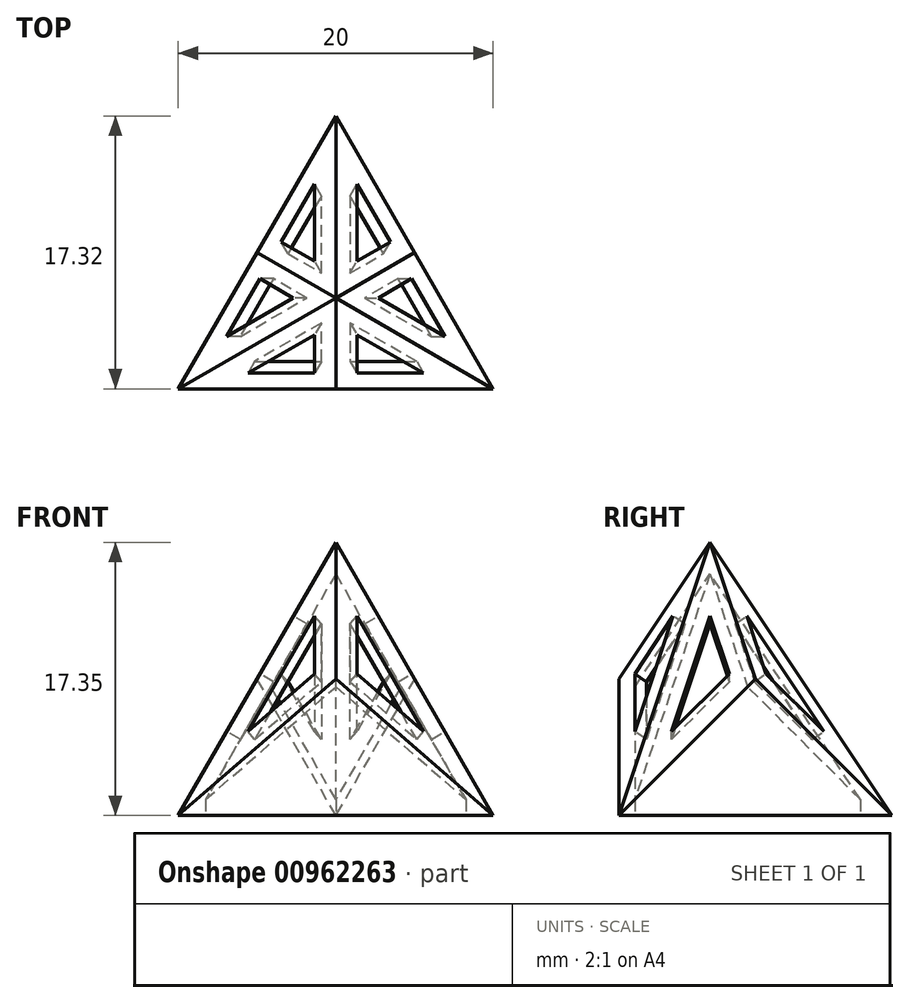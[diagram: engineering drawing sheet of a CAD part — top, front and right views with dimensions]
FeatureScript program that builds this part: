
annotation { "Feature Type Name" : "Feature", "Feature Type Description" : "" }
export const myFeature = defineFeature(function(context is Context, id is Id, definition is map)
    precondition{}
    {
        {
            var Q0;
            Q0=qCreatedBy(makeId("Top.planeOp"),FACE);
            var sketch = newSketch(context, id + "F0", { "sketchPlane" : qUnion([Q0])});
            skLineSegment(sketch, "E0", {"start": v(-10, -5.77) * mm, "end": v(0, 11.55) * mm});
            skLineSegment(sketch, "E1", {"start": v(0, 11.55) * mm, "end": v(10, -5.77) * mm});
            skLineSegment(sketch, "E2", {"start": v(10, -5.77) * mm, "end": v(-10, -5.77) * mm});
            skLineSegment(sketch, "E3", {"start": v(0, 0) * mm, "end": v(0, 11.55) * mm, "construction": true});
            skLineSegment(sketch, "E4", {"start": v(-10, -5.77) * mm, "end": v(0, 0) * mm, "construction": true});
            skLineSegment(sketch, "E5", {"start": v(10, -5.77) * mm, "end": v(0, 0) * mm, "construction": true});
            skSolve(sketch);
        }
        {
            var Q0;
            Q0 = qSketchRegion(id + "F0", true);
            extrude(context, id + "F1", {"entities" : qUnion([Q0]), "depth" : 17.35 * mm, "offsetDistance" : 25.4 * mm});
        }
        {
            var Q0;
            Q0=makeQuery(id+"F1.opExtrude","SWEPT_FACE",FACE,{"disambiguationData":[OSD([sQuery(id+"F0.wireOp",EDGE,"E0")])]});
            var sketch = newSketch(context, id + "F2", { "sketchPlane" : qUnion([Q0])});
            skLineSegment(sketch, "E6", {"start": v(-10, 0) * mm, "end": v(0, 17.35) * mm});
            skLineSegment(sketch, "E7", {"start": v(0, 17.35) * mm, "end": v(10, 0) * mm});
            skLineSegment(sketch, "E8", {"start": v(10, 0) * mm, "end": v(10, 17.35) * mm});
            skLineSegment(sketch, "E9", {"start": v(10, 17.35) * mm, "end": v(-10, 17.35) * mm});
            skLineSegment(sketch, "E10", {"start": v(-10, 17.35) * mm, "end": v(-10, 0) * mm});
            skSolve(sketch);
        }
        {
            var Q0;
            Q0 = qSketchRegion(id + "F2", true);
            extrude(context, id + "F3", {"entities" : qUnion([Q0]), "operationType" : NewBodyOperationType.REMOVE, "endBound" : BoundingType.THROUGH_ALL, "oppositeDirection" : true, "depth" : 25.4 * mm, "offsetDistance" : 25.4 * mm});
        }
        {
            var Q0;
            Q0=makeQuery(id+"F1.opExtrude","SWEPT_FACE",FACE,{"disambiguationData":[OSD([sQuery(id+"F0.wireOp",EDGE,"E2")])]});
            var sketch = newSketch(context, id + "F4", { "sketchPlane" : qUnion([Q0])});
            skLineSegment(sketch, "E11", {"start": v(-10, 0) * mm, "end": v(0, 17.35) * mm});
            skLineSegment(sketch, "E12", {"start": v(0, 17.35) * mm, "end": v(10, 0) * mm});
            skLineSegment(sketch, "E13", {"start": v(10, 0) * mm, "end": v(10, 17.35) * mm});
            skLineSegment(sketch, "E14", {"start": v(10, 17.35) * mm, "end": v(-10, 17.35) * mm});
            skLineSegment(sketch, "E15", {"start": v(-10, 17.35) * mm, "end": v(-10, 0) * mm});
            skSolve(sketch);
        }
        {
            var Q0;
            Q0 = qSketchRegion(id + "F4", true);
            extrude(context, id + "F5", {"entities" : qUnion([Q0]), "operationType" : NewBodyOperationType.REMOVE, "endBound" : BoundingType.THROUGH_ALL, "oppositeDirection" : true, "depth" : 25.4 * mm, "offsetDistance" : 25.4 * mm});
        }
        {
            var Q0;
            Q0=makeQuery(id+"F1.opExtrude","SWEPT_FACE",FACE,{"disambiguationData":[OSD([sQuery(id+"F0.wireOp",EDGE,"E1")])]});
            var sketch = newSketch(context, id + "F6", { "sketchPlane" : qUnion([Q0])});
            skLineSegment(sketch, "E16", {"start": v(-10, 0) * mm, "end": v(0, 17.35) * mm});
            skLineSegment(sketch, "E17", {"start": v(0, 17.35) * mm, "end": v(10, 0) * mm});
            skLineSegment(sketch, "E18", {"start": v(10, 0) * mm, "end": v(10, 17.35) * mm});
            skLineSegment(sketch, "E19", {"start": v(10, 17.35) * mm, "end": v(-10, 17.35) * mm});
            skLineSegment(sketch, "E20", {"start": v(-10, 17.35) * mm, "end": v(-10, 0) * mm});
            skSolve(sketch);
        }
        {
            var Q0;
            Q0 = qSketchRegion(id + "F6", true);
            extrude(context, id + "F7", {"entities" : qUnion([Q0]), "operationType" : NewBodyOperationType.REMOVE, "endBound" : BoundingType.THROUGH_ALL, "oppositeDirection" : true, "depth" : 25.4 * mm, "offsetDistance" : 25.4 * mm});
        }
        {
            var Q0;
            Q0=makeQuery(id+"F1.opExtrude","CAP_FACE",FACE,{"disambiguationData":[OSD([sQuery(id+"F0.wireOp",EDGE,"E0"),sQuery(id+"F0.wireOp",EDGE,"E1"),sQuery(id+"F0.wireOp",EDGE,"E2")])],"isStart":true});
            shell(context, id + "F8", {"entities" : qUnion([Q0]), "thickness" : 1 * mm});
        }
        {
            var Q0;
            Q0=makeQuery(id+"F5.boolean.opBoolean","COPY",FACE,{"derivedFrom":makeQuery(id+"F5.opExtrude","SWEPT_FACE",FACE,{"disambiguationData":[OSD([sQuery(id+"F4.wireOp",EDGE,"E12")])]})});
            var sketch = newSketch(context, id + "F9", { "sketchPlane" : qUnion([Q0])});
            skLineSegment(sketch, "E21.0", {"start": v(1.22, 5.38) * mm, "end": v(0, 9.62) * mm});
            skLineSegment(sketch, "E21.1", {"start": v(-2.44, 1.15) * mm, "end": v(1.22, 5.38) * mm});
            skLineSegment(sketch, "E21.2", {"start": v(0, 9.62) * mm, "end": v(-2.44, 1.15) * mm});
            skSolve(sketch);
        }
        {
            var Q0;
            Q0 = qSketchRegion(id + "F9", true);
            extrude(context, id + "F10", {"entities" : qUnion([Q0]), "operationType" : NewBodyOperationType.REMOVE, "endBound" : BoundingType.UP_TO_NEXT, "oppositeDirection" : true, "depth" : 25.4 * mm, "offsetDistance" : 25.4 * mm});
        }
        {
            var Q0;
            Q0=makeQuery(id+"F7.boolean.opBoolean","COPY",FACE,{"derivedFrom":makeQuery(id+"F7.opExtrude","SWEPT_FACE",FACE,{"disambiguationData":[OSD([sQuery(id+"F6.wireOp",EDGE,"E16")])]})});
            var sketch = newSketch(context, id + "F11", { "sketchPlane" : qUnion([Q0])});
            skLineSegment(sketch, "E22.0", {"start": v(-2.66, 4.84) * mm, "end": v(2.03, 1.78) * mm});
            skLineSegment(sketch, "E22.1", {"start": v(-2.66, 9.24) * mm, "end": v(-2.66, 4.84) * mm});
            skLineSegment(sketch, "E22.2", {"start": v(2.03, 1.78) * mm, "end": v(-2.66, 9.24) * mm});
            skSolve(sketch);
        }
        {
            var Q0;
            Q0 = qSketchRegion(id + "F11", true);
            extrude(context, id + "F12", {"entities" : qUnion([Q0]), "operationType" : NewBodyOperationType.REMOVE, "endBound" : BoundingType.UP_TO_NEXT, "oppositeDirection" : true, "depth" : 25.4 * mm, "offsetDistance" : 25.4 * mm});
        }
        {
            var Q0;
            Q0=makeQuery(id+"F3.boolean.opBoolean","COPY",FACE,{"derivedFrom":makeQuery(id+"F3.opExtrude","SWEPT_FACE",FACE,{"disambiguationData":[OSD([sQuery(id+"F2.wireOp",EDGE,"E7")])]})});
            var sketch = newSketch(context, id + "F13", { "sketchPlane" : qUnion([Q0])});
            skLineSegment(sketch, "E23.0", {"start": v(-2.03, 1.78) * mm, "end": v(2.66, 4.84) * mm});
            skLineSegment(sketch, "E23.1", {"start": v(2.66, 9.24) * mm, "end": v(-2.03, 1.78) * mm});
            skLineSegment(sketch, "E23.2", {"start": v(2.66, 4.84) * mm, "end": v(2.66, 9.24) * mm});
            skSolve(sketch);
        }
        {
            var Q0;
            Q0 = qSketchRegion(id + "F13", true);
            extrude(context, id + "F14", {"entities" : qUnion([Q0]), "operationType" : NewBodyOperationType.REMOVE, "endBound" : BoundingType.UP_TO_NEXT, "oppositeDirection" : true, "depth" : 25.4 * mm, "offsetDistance" : 25.4 * mm});
        }
        {
            var Q0;
            Q0=makeQuery(id+"F5.boolean.opBoolean","COPY",FACE,{"derivedFrom":makeQuery(id+"F5.opExtrude","SWEPT_FACE",FACE,{"disambiguationData":[OSD([sQuery(id+"F4.wireOp",EDGE,"E11")])]})});
            var sketch = newSketch(context, id + "F15", { "sketchPlane" : qUnion([Q0])});
            skLineSegment(sketch, "E24.0", {"start": v(2.44, 1.15) * mm, "end": v(0, 9.62) * mm});
            skLineSegment(sketch, "E24.1", {"start": v(-1.22, 5.38) * mm, "end": v(2.44, 1.15) * mm});
            skLineSegment(sketch, "E24.2", {"start": v(0, 9.62) * mm, "end": v(-1.22, 5.38) * mm});
            skSolve(sketch);
        }
        {
            var Q0;
            Q0 = qSketchRegion(id + "F15", true);
            extrude(context, id + "F16", {"entities" : qUnion([Q0]), "operationType" : NewBodyOperationType.REMOVE, "endBound" : BoundingType.UP_TO_NEXT, "oppositeDirection" : true, "depth" : 25.4 * mm, "offsetDistance" : 25.4 * mm});
        }
        {
            var Q0;
            Q0=makeQuery(id+"F3.boolean.opBoolean","COPY",FACE,{"derivedFrom":makeQuery(id+"F3.opExtrude","SWEPT_FACE",FACE,{"disambiguationData":[OSD([sQuery(id+"F2.wireOp",EDGE,"E6")])]})});
            var sketch = newSketch(context, id + "F17", { "sketchPlane" : qUnion([Q0])});
            skLineSegment(sketch, "E25.0", {"start": v(0.32, 5.51) * mm, "end": v(2.66, 0.43) * mm});
            skLineSegment(sketch, "E25.1", {"start": v(2.66, 9.24) * mm, "end": v(0.32, 5.51) * mm});
            skLineSegment(sketch, "E25.2", {"start": v(2.66, 0.43) * mm, "end": v(2.66, 9.24) * mm});
            skSolve(sketch);
        }
        {
            var Q0;
            Q0 = qSketchRegion(id + "F17", true);
            extrude(context, id + "F18", {"entities" : qUnion([Q0]), "operationType" : NewBodyOperationType.REMOVE, "endBound" : BoundingType.UP_TO_NEXT, "oppositeDirection" : true, "depth" : 25.4 * mm, "offsetDistance" : 25.4 * mm});
        }
        {
            var Q0;
            Q0=makeQuery(id+"F7.boolean.opBoolean","COPY",FACE,{"derivedFrom":makeQuery(id+"F7.opExtrude","SWEPT_FACE",FACE,{"disambiguationData":[OSD([sQuery(id+"F6.wireOp",EDGE,"E17")])]})});
            var sketch = newSketch(context, id + "F19", { "sketchPlane" : qUnion([Q0])});
            skLineSegment(sketch, "E26.0", {"start": v(-2.66, 0.43) * mm, "end": v(-0.32, 5.51) * mm});
            skLineSegment(sketch, "E26.1", {"start": v(-2.66, 9.24) * mm, "end": v(-2.66, 0.43) * mm});
            skLineSegment(sketch, "E26.2", {"start": v(-0.32, 5.51) * mm, "end": v(-2.66, 9.24) * mm});
            skSolve(sketch);
        }
        {
            var Q0;
            Q0 = qSketchRegion(id + "F19", true);
            extrude(context, id + "F20", {"entities" : qUnion([Q0]), "operationType" : NewBodyOperationType.REMOVE, "endBound" : BoundingType.UP_TO_NEXT, "oppositeDirection" : true, "depth" : 25.4 * mm, "offsetDistance" : 25.4 * mm});
        }
    });
